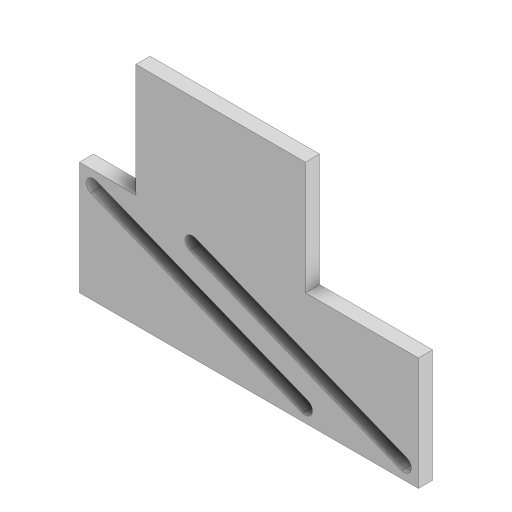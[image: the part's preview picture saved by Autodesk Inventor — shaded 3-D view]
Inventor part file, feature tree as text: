
AUTODESK INVENTOR PART (.ipt)
format: ipt  version: 2024.2 (Build 282272000, 272)  size: 123,904 bytes
history: native  units: in
note: dims shown in document units (in); Inventor stores cm internally (conversion verified against a paired STEP export)
features: extrude x1, sketch x1
ambient origin geometry x8: Origin, YZ Plane, XZ Plane, XY Plane, X Axis, Y Axis, Z Axis, Center Point
bodies: Solid1 (feature_tree)
feature tree (2):
  extrude  "Extrusion1"  Depth=2.0in
  sketch  "Sketch2"  dims[d0=3.0in d1=2.0in d2=6.0in d3=2.0in d4=1.0in d5=0.25in d6=0.25in d7=0.25in d8=0.25in d9=0.25in d10=0.25in d11=0.25in d12=0.25in d13=0.25in d14=0.0in]
